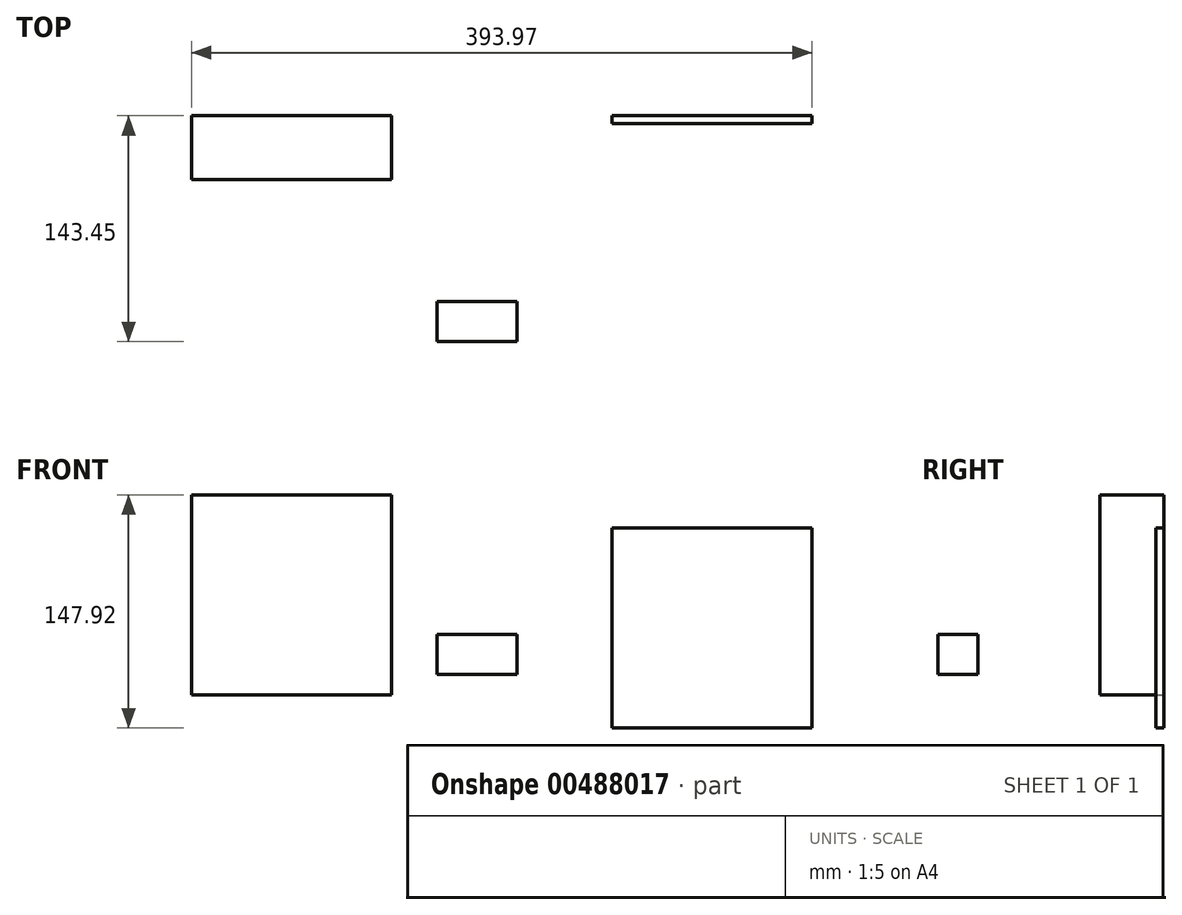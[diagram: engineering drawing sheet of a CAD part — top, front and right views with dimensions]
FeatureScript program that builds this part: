
annotation { "Feature Type Name" : "Feature", "Feature Type Description" : "" }
export const myFeature = defineFeature(function(context is Context, id is Id, definition is map)
    precondition{}
    {
        {
            var Q0;
            Q0=qCreatedBy(makeId("Front.planeOp"),FACE);
            var sketch = newSketch(context, id + "F0", { "sketchPlane" : qUnion([Q0])});
            skLineSegment(sketch, "E0.bottom", {"start": v(-155.84, 135.14) * mm, "end": v(-28.84, 135.14) * mm});
            skLineSegment(sketch, "E0.top", {"start": v(-155.84, 8.14) * mm, "end": v(-28.84, 8.14) * mm});
            skLineSegment(sketch, "E0.left", {"start": v(-155.84, 135.14) * mm, "end": v(-155.84, 8.14) * mm});
            skLineSegment(sketch, "E0.right", {"start": v(-28.84, 135.14) * mm, "end": v(-28.84, 8.14) * mm});
            skSolve(sketch);
        }
        {
            var Q0;
            Q0=makeQuery(id+"F0.imprint","IMPRINT",FACE,{"disambiguationData":[TD([[makeQuery(id+"F0.imprint","IMPRINT",EDGE,{"derivedFrom":sQuery(id+"F0.wireOp",EDGE,"E0.bottom")}),-1.0]])]});
            extrude(context, id + "F1", {"entities" : qUnion([Q0]), "depth" : 40.64 * mm});
        }
        {
            var Q0;
            Q0=qCreatedBy(makeId("Right.planeOp"),FACE);
            var sketch = newSketch(context, id + "F2", { "sketchPlane" : qUnion([Q0])});
            skLineSegment(sketch, "E1.bottom", {"start": v(-143.45, 46.48) * mm, "end": v(-118.05, 46.48) * mm});
            skLineSegment(sketch, "E1.top", {"start": v(-143.45, 21.08) * mm, "end": v(-118.05, 21.08) * mm});
            skLineSegment(sketch, "E1.left", {"start": v(-143.45, 46.48) * mm, "end": v(-143.45, 21.08) * mm});
            skLineSegment(sketch, "E1.right", {"start": v(-118.05, 46.48) * mm, "end": v(-118.05, 21.08) * mm});
            skSolve(sketch);
        }
        {
            var Q0;
            Q0=makeQuery(id+"F2.imprint","IMPRINT",FACE,{"disambiguationData":[TD([[makeQuery(id+"F2.imprint","IMPRINT",EDGE,{"derivedFrom":sQuery(id+"F2.wireOp",EDGE,"E1.bottom")}),-1.0]])]});
            extrude(context, id + "F3", {"entities" : qUnion([Q0]), "depth" : 50.8 * mm});
        }
        {
            var Q0;
            Q0=qCreatedBy(makeId("Front.planeOp"),FACE);
            var sketch = newSketch(context, id + "F4", { "sketchPlane" : qUnion([Q0])});
            skLineSegment(sketch, "E2.bottom", {"start": v(238.13, 114.22) * mm, "end": v(111.13, 114.22) * mm});
            skLineSegment(sketch, "E2.top", {"start": v(238.13, -12.78) * mm, "end": v(111.13, -12.78) * mm});
            skLineSegment(sketch, "E2.left", {"start": v(238.13, 114.22) * mm, "end": v(238.13, -12.78) * mm});
            skLineSegment(sketch, "E2.right", {"start": v(111.13, 114.22) * mm, "end": v(111.13, -12.78) * mm});
            skSolve(sketch);
        }
        {
            var Q0;
            Q0 = qSketchRegion(id + "F4", true);
            extrude(context, id + "F5", {"entities" : qUnion([Q0]), "depth" : 5.08 * mm});
        }
    });
